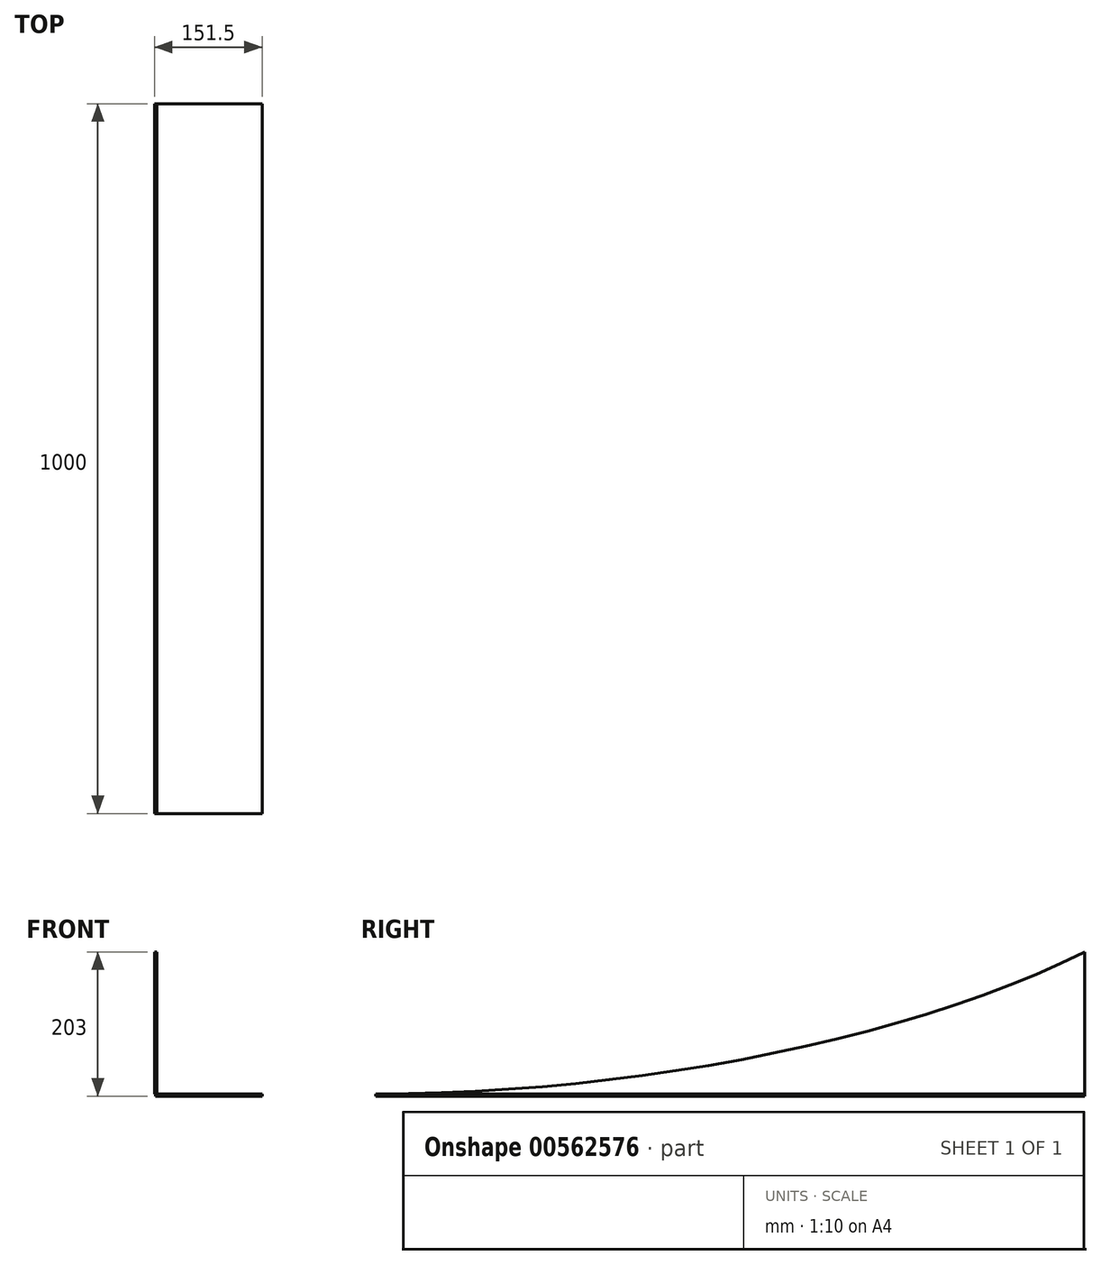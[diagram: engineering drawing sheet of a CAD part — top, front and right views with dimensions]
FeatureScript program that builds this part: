
annotation { "Feature Type Name" : "Feature", "Feature Type Description" : "" }
export const myFeature = defineFeature(function(context is Context, id is Id, definition is map)
    precondition{}
    {
        {
            var Q0;
            Q0=qCreatedBy(makeId("Right.planeOp"),FACE);
            var sketch = newSketch(context, id + "F0", { "sketchPlane" : qUnion([Q0])});
            skFitSpline(sketch, "E0", {"points": [v(-507.58, -64.46) * mm, v(492.42, 135.54) * mm], "startDerivative": vector(1064.65, 0) * mm, "endDerivative": vector(757.35, 377.28) * mm});
            skLineSegment(sketch, "E1", {"start": v(-507.58, -64.46) * mm, "end": v(492.42, -64.46) * mm});
            skLineSegment(sketch, "E2", {"start": v(492.42, -64.46) * mm, "end": v(492.42, 135.54) * mm});
            skSolve(sketch);
        }
        {
            var Q0;
            Q0=makeQuery(id+"F0.imprint","IMPRINT",FACE,{"disambiguationData":[TD([[makeQuery(id+"F0.imprint","IMPRINT",EDGE,{"derivedFrom":sQuery(id+"F0.wireOp",EDGE,"E0")}),-1.0]])]});
            extrude(context, id + "F1", {"entities" : qUnion([Q0]), "endBound" : BoundingType.SYMMETRIC, "depth" : 3 * mm, "offsetDistance" : 25 * mm});
        }
        {
            var Q0;
            Q0=sQuery(id+"F0.wireOp",EDGE,"E1");
            extrude(context, id + "F2", {"bodyType" : ToolBodyType.SURFACE, "surfaceEntities" : qUnion([Q0]), "depth" : 150 * mm, "offsetDistance" : 25 * mm});
        }
        {
            var Q0;
            Q0=makeQuery(id+"F2.opExtrude","SWEPT_FACE",FACE,{"disambiguationData":[OSD([sQuery(id+"F0.wireOp",EDGE,"E1")])]});
            extrude(context, id + "F3", {"entities" : qUnion([Q0]), "operationType" : NewBodyOperationType.ADD, "depth" : 3 * mm, "offsetDistance" : 25 * mm});
        }
    });
